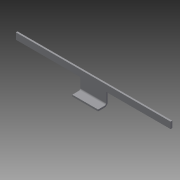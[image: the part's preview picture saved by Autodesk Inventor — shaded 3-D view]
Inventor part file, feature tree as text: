
AUTODESK INVENTOR PART (.ipt)
format: ipt  version: 2013 (Build 170138000, 138)  size: 159,744 bytes
history: native  units: in
note: dims shown in document units (in); Inventor stores cm internally (conversion verified against a paired STEP export)
features: sheet_metal_op x8, sketch x5, other x5, reference x5
ambient origin geometry x8: Origin, YZ Plane, XZ Plane, XY Plane, X Axis, Y Axis, Z Axis, Center Point
bodies: Solid1 (feature_tree)
feature tree (23):
  sheet_metal_op  "Face1"
  sheet_metal_op  "Flange1"
  sheet_metal_op  "Face2"
  sheet_metal_op  "Face3"
  sketch  "Sketch1"  dims[d0=0.5in]
  other  "Plate1"
  sketch  "Sketch2"  dims[d1=2.0in]
  other  "Plate2"
  sheet_metal_op  "Bend1"
  sheet_metal_op  "Corner1"
  sketch  "Sketch3"  dims[d2=0.125in]
  other  "Plate3"
  sheet_metal_op  "Bend2"
  sketch  "Sketch4"  dims[d3=0.125in]
  reference  "Reference1"
  reference  "Reference2"
  reference  "Reference3"
  reference  "Reference4"
  sketch  "Sketch5"  dims[d4=0.0625in d5=0.25in d6=0.125in d7=1.75in d8=90.0deg d9=0.125in d10=0.5in d11=0.125in d12=0.125in d13=2.0in d14=0.5in d15=2.0in d16=0.125in d17=0.125in d18=0.0625in d19=0.25in d20=0.125in d21=0.125in d22=0.0in d23=0.25in d25=0.0625in d27=0.25in d28=0.25in d29=0.0625in d30=0.0625in d31=0.125in d32=0.125in d33=0.0625in d34=0.25in d35=0.125in d36=1.0in d37=0.25in d38=0.0625in]
  reference  "Reference5"
  other  "Plate4"
  sheet_metal_op  "Bend3"
  other  "Cut1"
